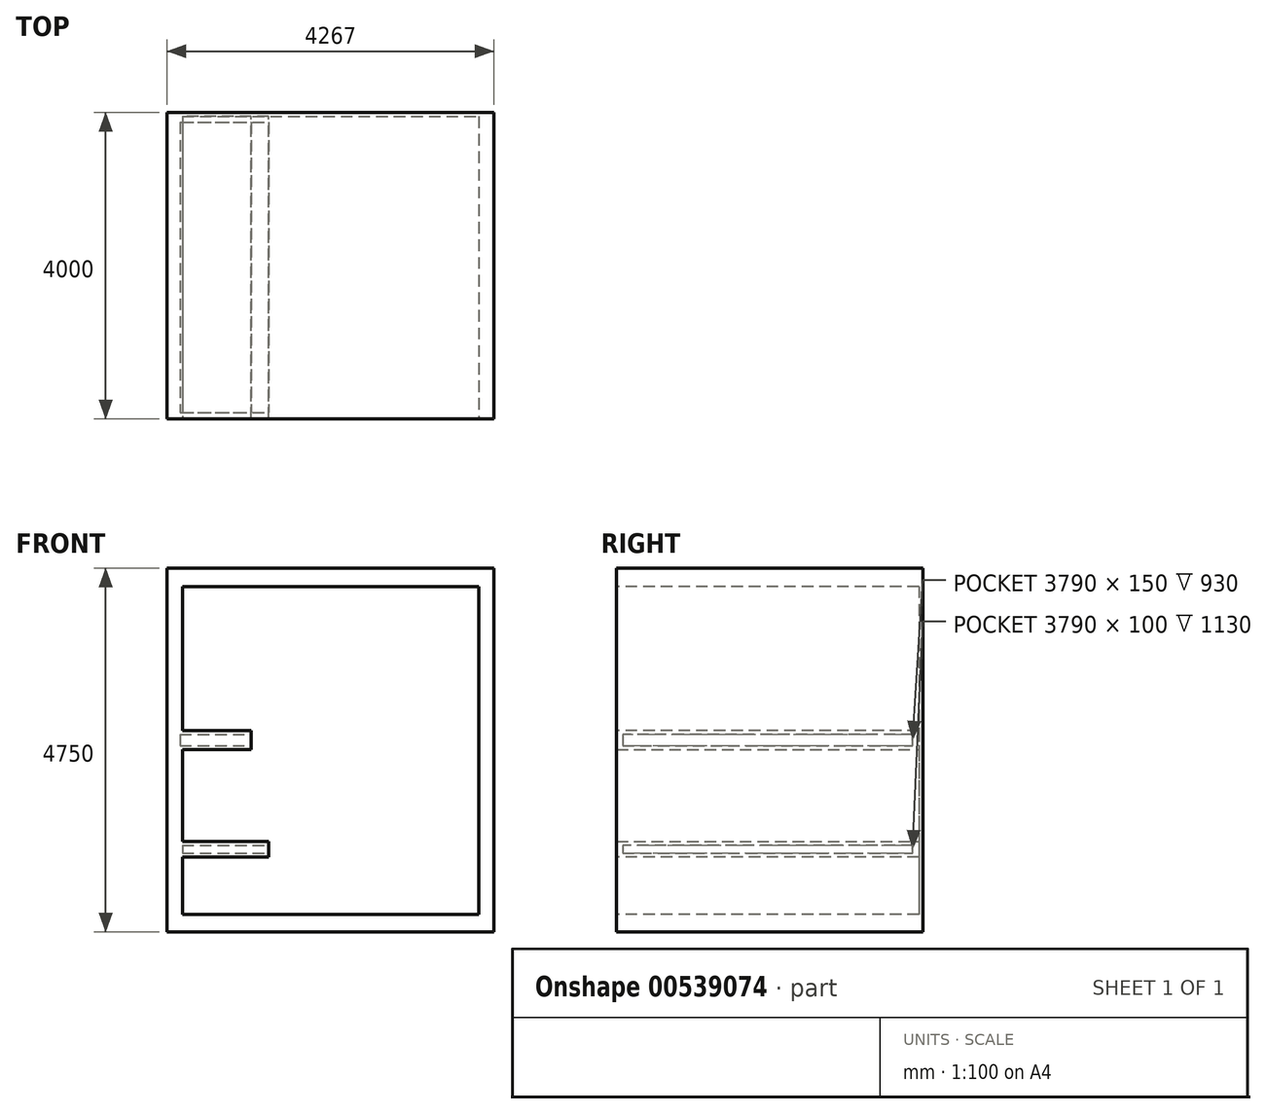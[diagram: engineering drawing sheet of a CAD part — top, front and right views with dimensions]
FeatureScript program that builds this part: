
annotation { "Feature Type Name" : "Feature", "Feature Type Description" : "" }
export const myFeature = defineFeature(function(context is Context, id is Id, definition is map)
    precondition{}
    {
        {
            var Q0;
            Q0=qCreatedBy(makeId("Top.planeOp"),FACE);
            var sketch = newSketch(context, id + "F0", { "sketchPlane" : qUnion([Q0])});
            skLineSegment(sketch, "E0", {"start": v(0, 4000) * mm, "end": v(0, 0) * mm});
            skLineSegment(sketch, "E1", {"start": v(0, 0) * mm, "end": v(4267, 0) * mm});
            skLineSegment(sketch, "E2", {"start": v(4267, 0) * mm, "end": v(4267, 4000) * mm});
            skLineSegment(sketch, "E3", {"start": v(4267, 4000) * mm, "end": v(0, 4000) * mm});
            skSolve(sketch);
        }
        {
            var Q0;
            Q0 = qSketchRegion(id + "F0", true);
            extrude(context, id + "F1", {"entities" : qUnion([Q0]), "depth" : 4750 * mm, "offsetDistance" : 25 * mm});
        }
        {
            var Q0;
            Q0=makeQuery(id+"F1.opExtrude","SWEPT_FACE",FACE,{"disambiguationData":[OSD([sQuery(id+"F0.wireOp",EDGE,"E1")])]});
            var sketch = newSketch(context, id + "F2", { "sketchPlane" : qUnion([Q0])});
            skLineSegment(sketch, "E4.bottom", {"start": v(200, 4510) * mm, "end": v(4067, 4510) * mm});
            skLineSegment(sketch, "E4.top", {"start": v(200, 230) * mm, "end": v(4067, 230) * mm});
            skLineSegment(sketch, "E4.left", {"start": v(200, 4510) * mm, "end": v(200, 230) * mm});
            skLineSegment(sketch, "E4.right", {"start": v(4067, 4510) * mm, "end": v(4067, 230) * mm});
            skSolve(sketch);
        }
        {
            var Q0;
            Q0 = qSketchRegion(id + "F2", true);
            extrude(context, id + "F3", {"entities" : qUnion([Q0]), "operationType" : NewBodyOperationType.REMOVE, "oppositeDirection" : true, "depth" : 3950 * mm, "offsetDistance" : 25 * mm});
        }
        {
            var Q0;
            Q0=makeQuery(id+"F3.boolean.opBoolean","COPY",FACE,{"derivedFrom":makeQuery(id+"F3.opExtrude","SWEPT_FACE",FACE,{"disambiguationData":[OSD([sQuery(id+"F2.wireOp",EDGE,"E4.left")])]})});
            var sketch = newSketch(context, id + "F4", { "sketchPlane" : qUnion([Q0])});
            skLineSegment(sketch, "E5", {"start": v(0, 1180) * mm, "end": v(3950, 1180) * mm});
            skLineSegment(sketch, "E6", {"start": v(3950, 1180) * mm, "end": v(3950, 980) * mm});
            skLineSegment(sketch, "E7", {"start": v(3950, 980) * mm, "end": v(0, 980) * mm});
            skLineSegment(sketch, "E8", {"start": v(0, 980) * mm, "end": v(0, 1180) * mm});
            skSolve(sketch);
        }
        {
            var Q0;
            Q0 = qSketchRegion(id + "F4", true);
            extrude(context, id + "F5", {"entities" : qUnion([Q0]), "operationType" : NewBodyOperationType.ADD, "depth" : 1130 * mm, "offsetDistance" : 25 * mm});
        }
        {
            var Q0;
            {var subQ0=sQuery(id+"F2.wireOp",EDGE,"E4.left");var subQ1=sQuery(id+"F2.wireOp",EDGE,"E4.bottom");Q0=makeQuery(id+"F5.boolean.opBoolean","SPLIT",FACE,{"disambiguationData":[TD([makeQuery(id+"F3.boolean.opBoolean","COPY",FACE,{"derivedFrom":makeQuery(id+"F3.opExtrude","SWEPT_FACE",FACE,{"disambiguationData":[OSD([subQ1])]})})])],"derivedFrom":makeQuery(id+"F3.boolean.opBoolean","COPY",FACE,{"derivedFrom":makeQuery(id+"F3.opExtrude","SWEPT_FACE",FACE,{"disambiguationData":[OSD([subQ0])]})})});}
            var sketch = newSketch(context, id + "F6", { "sketchPlane" : qUnion([Q0])});
            skLineSegment(sketch, "E9", {"start": v(0, 2630) * mm, "end": v(0, 2380) * mm});
            skLineSegment(sketch, "E10", {"start": v(0, 2380) * mm, "end": v(3950, 2380) * mm});
            skLineSegment(sketch, "E11", {"start": v(3950, 2380) * mm, "end": v(3950, 2630) * mm});
            skLineSegment(sketch, "E12", {"start": v(3950, 2630) * mm, "end": v(0, 2630) * mm});
            skSolve(sketch);
        }
        {
            var Q0;
            Q0 = qSketchRegion(id + "F6", true);
            extrude(context, id + "F7", {"entities" : qUnion([Q0]), "operationType" : NewBodyOperationType.ADD, "depth" : 900 * mm, "offsetDistance" : 25 * mm});
        }
        {
            var Q0;
            Q0=makeQuery(id+"F7.opExtrude","CAP_FACE",FACE,{"disambiguationData":[OSD([sQuery(id+"F6.wireOp",EDGE,"E9"),sQuery(id+"F6.wireOp",EDGE,"E10"),sQuery(id+"F6.wireOp",EDGE,"E11"),sQuery(id+"F6.wireOp",EDGE,"E12")])],"isStart":false});
            var sketch = newSketch(context, id + "F8", { "sketchPlane" : qUnion([Q0])});
            skLineSegment(sketch, "E13", {"start": v(80, 2580) * mm, "end": v(80, 2430) * mm});
            skLineSegment(sketch, "E14", {"start": v(80, 2430) * mm, "end": v(3870, 2430) * mm});
            skLineSegment(sketch, "E15", {"start": v(3870, 2430) * mm, "end": v(3870, 2580) * mm});
            skLineSegment(sketch, "E16", {"start": v(3870, 2580) * mm, "end": v(80, 2580) * mm});
            skSolve(sketch);
        }
        {
            var Q0;
            Q0 = qSketchRegion(id + "F8", true);
            extrude(context, id + "F9", {"entities" : qUnion([Q0]), "operationType" : NewBodyOperationType.REMOVE, "oppositeDirection" : true, "depth" : 930 * mm, "offsetDistance" : 25 * mm});
        }
        {
            var Q0;
            Q0=makeQuery(id+"F5.opExtrude","CAP_FACE",FACE,{"disambiguationData":[OSD([sQuery(id+"F4.wireOp",EDGE,"E5"),sQuery(id+"F4.wireOp",EDGE,"E6"),sQuery(id+"F4.wireOp",EDGE,"E7"),sQuery(id+"F4.wireOp",EDGE,"E8")])],"isStart":false});
            var sketch = newSketch(context, id + "F10", { "sketchPlane" : qUnion([Q0])});
            skLineSegment(sketch, "E17", {"start": v(80, 1130) * mm, "end": v(80, 1030) * mm});
            skLineSegment(sketch, "E18", {"start": v(80, 1030) * mm, "end": v(3870, 1030) * mm});
            skLineSegment(sketch, "E19", {"start": v(3870, 1030) * mm, "end": v(3870, 1130) * mm});
            skLineSegment(sketch, "E20", {"start": v(3870, 1130) * mm, "end": v(80, 1130) * mm});
            skSolve(sketch);
        }
        {
            var Q0;
            Q0 = qSketchRegion(id + "F10", true);
            extrude(context, id + "F11", {"entities" : qUnion([Q0]), "operationType" : NewBodyOperationType.REMOVE, "oppositeDirection" : true, "depth" : 1130 * mm, "offsetDistance" : 25 * mm});
        }
    });
